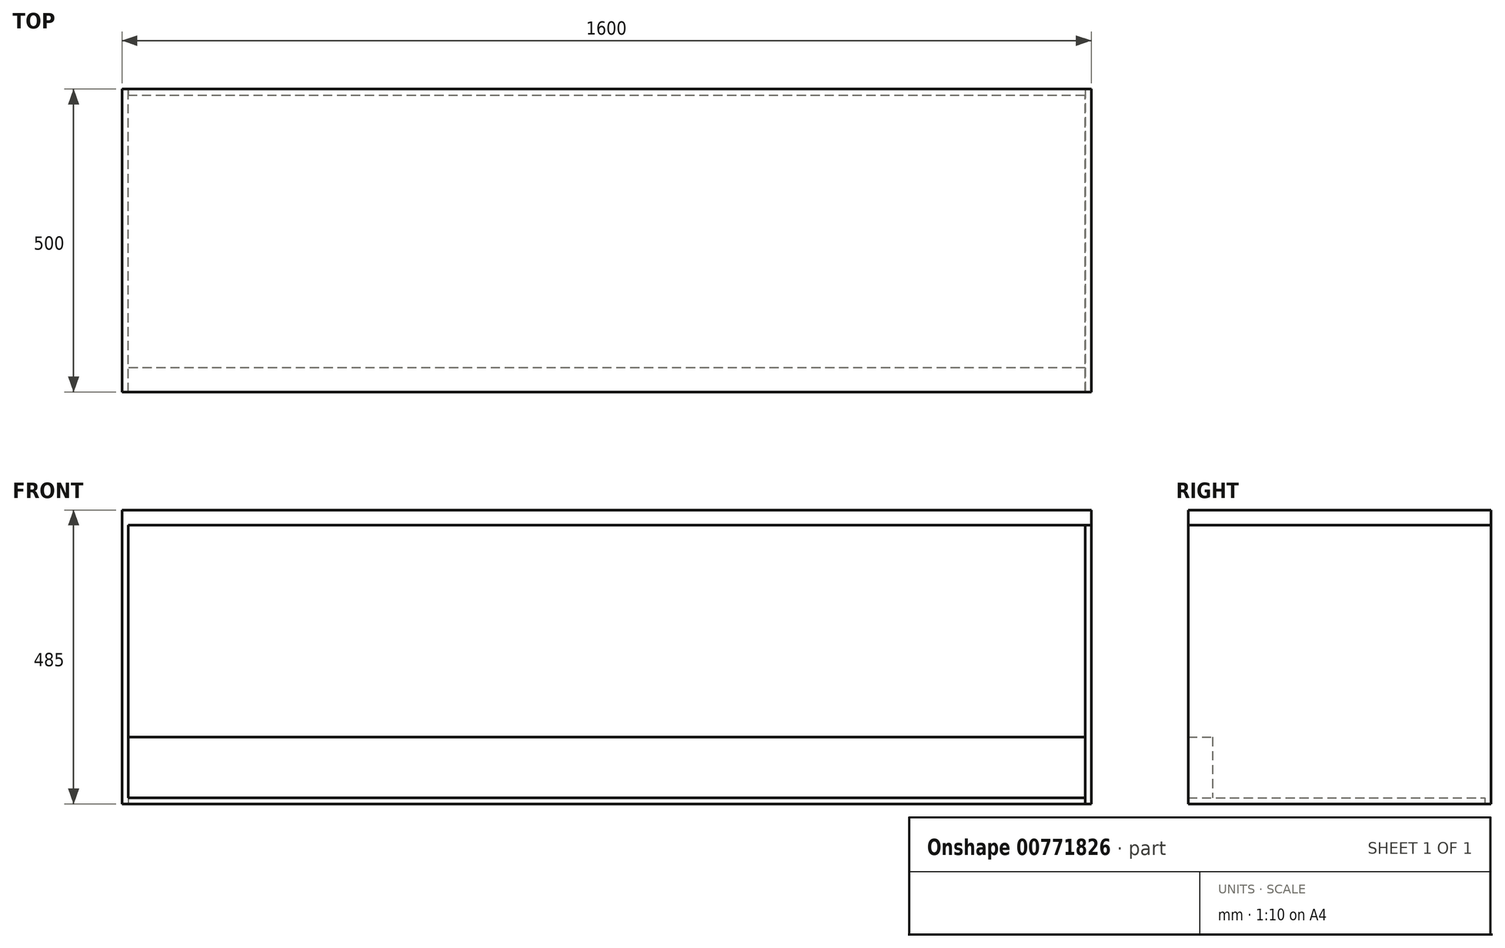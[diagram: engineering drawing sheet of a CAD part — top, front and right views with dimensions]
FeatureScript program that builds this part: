
annotation { "Feature Type Name" : "Feature", "Feature Type Description" : "" }
export const myFeature = defineFeature(function(context is Context, id is Id, definition is map)
    precondition{}
    {
        {
            var Q0;
            Q0=qCreatedBy(makeId("Top.planeOp"),FACE);
            var sketch = newSketch(context, id + "F0", { "sketchPlane" : qUnion([Q0])});
            skLineSegment(sketch, "E0.bottom", {"start": v(0, 0) * mm, "end": v(1600, 0) * mm});
            skLineSegment(sketch, "E0.top", {"start": v(0, 500) * mm, "end": v(1600, 500) * mm});
            skLineSegment(sketch, "E0.left", {"start": v(0, 0) * mm, "end": v(0, 500) * mm});
            skLineSegment(sketch, "E0.right", {"start": v(1600, 0) * mm, "end": v(1600, 500) * mm});
            skSolve(sketch);
        }
        {
            var Q0;
            Q0=makeQuery(id+"F0.imprint","IMPRINT",FACE,{"disambiguationData":[TD([[makeQuery(id+"F0.imprint","IMPRINT",EDGE,{"derivedFrom":sQuery(id+"F0.wireOp",EDGE,"E0.bottom")}),1.0]])]});
            extrude(context, id + "F1", {"entities" : qUnion([Q0]), "depth" : 25 * mm, "offsetDistance" : 25 * mm});
        }
        {
            var Q0;
            Q0=makeQuery(id+"F0.imprint","IMPRINT",FACE,{"disambiguationData":[TD([[makeQuery(id+"F0.imprint","IMPRINT",EDGE,{"derivedFrom":sQuery(id+"F0.wireOp",EDGE,"E0.bottom")}),1.0]])]});
            cPlane(context, id + "F2", {"entities" : qUnion([Q0]), "cplaneType" : CPlaneType.OFFSET, "offset" : 460 * mm, "oppositeDirection" : true, "width" : 150 * mm, "height" : 150 * mm});
        }
        {
            var Q0;
            Q0=qCreatedBy(id+"F2.planeOp",FACE);
            var sketch = newSketch(context, id + "F3", { "sketchPlane" : qUnion([Q0])});
            skLineSegment(sketch, "E1.bottom", {"start": v(10, 0) * mm, "end": v(1590, 0) * mm});
            skLineSegment(sketch, "E1.top", {"start": v(10, 490) * mm, "end": v(1590, 490) * mm});
            skLineSegment(sketch, "E1.left", {"start": v(10, 0) * mm, "end": v(10, 490) * mm});
            skLineSegment(sketch, "E1.right", {"start": v(1590, 0) * mm, "end": v(1590, 490) * mm});
            skSolve(sketch);
        }
        {
            var Q0;
            Q0=makeQuery(id+"F3.imprint","IMPRINT",FACE,{"disambiguationData":[TD([[makeQuery(id+"F3.imprint","IMPRINT",EDGE,{"derivedFrom":sQuery(id+"F3.wireOp",EDGE,"E1.bottom")}),1.0]])]});
            extrude(context, id + "F4", {"entities" : qUnion([Q0]), "depth" : 10 * mm, "offsetDistance" : 25 * mm});
        }
        {
            var Q0;
            Q0=makeQuery(id+"F0.imprint","IMPRINT",FACE,{"disambiguationData":[TD([[makeQuery(id+"F0.imprint","IMPRINT",EDGE,{"derivedFrom":sQuery(id+"F0.wireOp",EDGE,"E0.bottom")}),1.0]])]});
            var sketch = newSketch(context, id + "F5", { "sketchPlane" : qUnion([Q0])});
            skLineSegment(sketch, "E2.bottom", {"start": v(0, 0) * mm, "end": v(10, 0) * mm});
            skLineSegment(sketch, "E2.top", {"start": v(0, 500) * mm, "end": v(10, 500) * mm});
            skLineSegment(sketch, "E2.left", {"start": v(0, 0) * mm, "end": v(0, 500) * mm});
            skLineSegment(sketch, "E2.right", {"start": v(10, 0) * mm, "end": v(10, 500) * mm});
            skSolve(sketch);
        }
        {
            var Q0;
            Q0=qSketchRegion(id+"F5",true);
            var Q1;
            Q1=makeQuery(id+"F4.opExtrude","CAP_FACE",FACE,{"disambiguationData":[OSD([sQuery(id+"F3.wireOp",EDGE,"E1.bottom"),sQuery(id+"F3.wireOp",EDGE,"E1.top"),sQuery(id+"F3.wireOp",EDGE,"E1.left"),sQuery(id+"F3.wireOp",EDGE,"E1.right")])],"isStart":true});
            extrude(context, id + "F6", {"entities" : qUnion([Q0]), "operationType" : NewBodyOperationType.ADD, "endBound" : BoundingType.UP_TO_SURFACE, "oppositeDirection" : true, "depth" : 25 * mm, "endBoundEntityFace" : qUnion([Q1]), "offsetDistance" : 25 * mm});
        }
        {
            var Q0;
            Q0=makeQuery(id+"F0.imprint","IMPRINT",FACE,{"disambiguationData":[TD([[makeQuery(id+"F0.imprint","IMPRINT",EDGE,{"derivedFrom":sQuery(id+"F0.wireOp",EDGE,"E0.bottom")}),1.0]])]});
            var sketch = newSketch(context, id + "F7", { "sketchPlane" : qUnion([Q0])});
            skLineSegment(sketch, "E3.bottom", {"start": v(1600, 0) * mm, "end": v(1590, 0) * mm});
            skLineSegment(sketch, "E3.top", {"start": v(1600, 500) * mm, "end": v(1590, 500) * mm});
            skLineSegment(sketch, "E3.left", {"start": v(1600, 0) * mm, "end": v(1600, 500) * mm});
            skLineSegment(sketch, "E3.right", {"start": v(1590, 0) * mm, "end": v(1590, 500) * mm});
            skSolve(sketch);
        }
        {
            var Q0;
            Q0=makeQuery(id+"F7.imprint","IMPRINT",FACE,{"disambiguationData":[TD([[makeQuery(id+"F7.imprint","IMPRINT",EDGE,{"derivedFrom":sQuery(id+"F7.wireOp",EDGE,"E3.bottom")}),1.0]])]});
            var Q1;
            Q1=makeQuery(id+"F4.opExtrude","CAP_FACE",FACE,{"disambiguationData":[OSD([sQuery(id+"F3.wireOp",EDGE,"E1.bottom"),sQuery(id+"F3.wireOp",EDGE,"E1.top"),sQuery(id+"F3.wireOp",EDGE,"E1.left"),sQuery(id+"F3.wireOp",EDGE,"E1.right")])],"isStart":true});
            extrude(context, id + "F8", {"entities" : qUnion([Q0]), "endBound" : BoundingType.UP_TO_SURFACE, "oppositeDirection" : true, "depth" : 25 * mm, "endBoundEntityFace" : qUnion([Q1]), "offsetDistance" : 25 * mm});
        }
        {
            var Q0;
            Q0=makeQuery(id+"F6.opExtrude","SWEPT_FACE",FACE,{"disambiguationData":[OSD([sQuery(id+"F5.wireOp",EDGE,"E2.right")])]});
            var sketch = newSketch(context, id + "F9", { "sketchPlane" : qUnion([Q0])});
            skLineSegment(sketch, "E4.bottom", {"start": v(0, -350) * mm, "end": v(40, -350) * mm});
            skLineSegment(sketch, "E4.top", {"start": v(0, -450) * mm, "end": v(40, -450) * mm});
            skLineSegment(sketch, "E4.left", {"start": v(0, -350) * mm, "end": v(0, -450) * mm});
            skLineSegment(sketch, "E4.right", {"start": v(40, -350) * mm, "end": v(40, -450) * mm});
            skSolve(sketch);
        }
        {
            var Q0;
            Q0=makeQuery(id+"F9.imprint","IMPRINT",FACE,{"disambiguationData":[TD([[makeQuery(id+"F9.imprint","IMPRINT",EDGE,{"derivedFrom":sQuery(id+"F9.wireOp",EDGE,"E4.bottom")}),-1.0]])]});
            extrude(context, id + "F10", {"entities" : qUnion([Q0]), "endBound" : BoundingType.UP_TO_NEXT, "depth" : 25 * mm, "offsetDistance" : 25 * mm});
        }
    });
